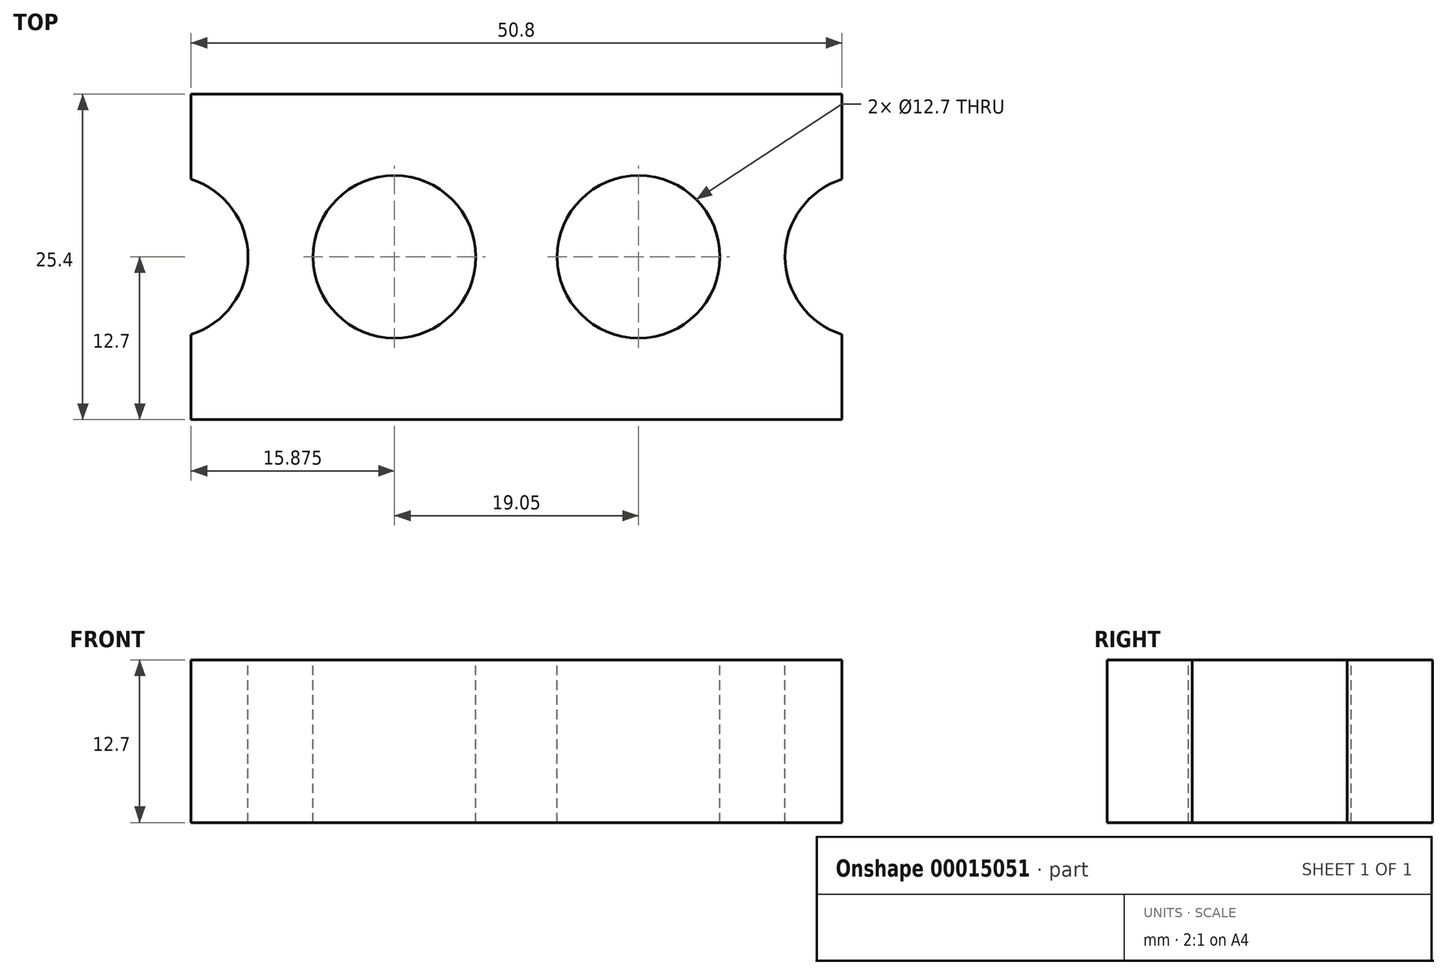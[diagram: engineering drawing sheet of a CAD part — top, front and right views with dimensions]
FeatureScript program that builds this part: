
annotation { "Feature Type Name" : "Feature", "Feature Type Description" : "" }
export const myFeature = defineFeature(function(context is Context, id is Id, definition is map)
    precondition{}
    {
        {
            var Q0;
            Q0=qCreatedBy(makeId("Top.planeOp"),FACE);
            var sketch = newSketch(context, id + "F0", { "sketchPlane" : qUnion([Q0])});
            skLineSegment(sketch, "E0.bottom", {"start": v(-25.4, 12.7) * mm, "end": v(25.4, 12.7) * mm});
            skLineSegment(sketch, "E0.top", {"start": v(-25.4, -12.7) * mm, "end": v(25.4, -12.7) * mm});
            skLineSegment(sketch, "E0.left", {"start": v(-25.4, 12.7) * mm, "end": v(-25.4, -12.7) * mm});
            skLineSegment(sketch, "E0.right", {"start": v(25.4, 12.7) * mm, "end": v(25.4, -12.7) * mm});
            skLineSegment(sketch, "E1", {"start": v(-25.4, -12.7) * mm, "end": v(25.4, 12.7) * mm, "construction": true});
            skSolve(sketch);
        }
        {
            var Q0;
            Q0 = qSketchRegion(id + "F0", true);
            extrude(context, id + "F1", {"entities" : qUnion([Q0]), "endBound" : BoundingType.SYMMETRIC, "depth" : 12.7 * mm});
        }
        {
            var Q0;
            Q0=makeQuery(id+"F1.opExtrude","CAP_FACE",FACE,{"disambiguationData":[OSD([sQuery(id+"F0.wireOp",EDGE,"E0.bottom"),sQuery(id+"F0.wireOp",EDGE,"E0.top"),sQuery(id+"F0.wireOp",EDGE,"E0.left"),sQuery(id+"F0.wireOp",EDGE,"E0.right")])],"isStart":false});
            var sketch = newSketch(context, id + "F2", { "sketchPlane" : qUnion([Q0])});
            skCircle(sketch, "E2", {"center": v(-27.3, 0) * mm, "radius": 6.35 * mm});
            skCircle(sketch, "E3", {"center": v(-9.53, 0) * mm, "radius": 6.35 * mm});
            skCircle(sketch, "E4", {"center": v(27.3, 0) * mm, "radius": 6.35 * mm});
            skCircle(sketch, "E5", {"center": v(9.53, 0) * mm, "radius": 6.35 * mm});
            skLineSegment(sketch, "E6", {"start": v(-9.53, 0) * mm, "end": v(9.53, 0) * mm, "construction": true});
            skSolve(sketch);
        }
        {
            var Q0;
            Q0 = qSketchRegion(id + "F2", true);
            extrude(context, id + "F3", {"entities" : qUnion([Q0]), "operationType" : NewBodyOperationType.REMOVE, "endBound" : BoundingType.THROUGH_ALL, "oppositeDirection" : true, "depth" : 25.4 * mm});
        }
    });
